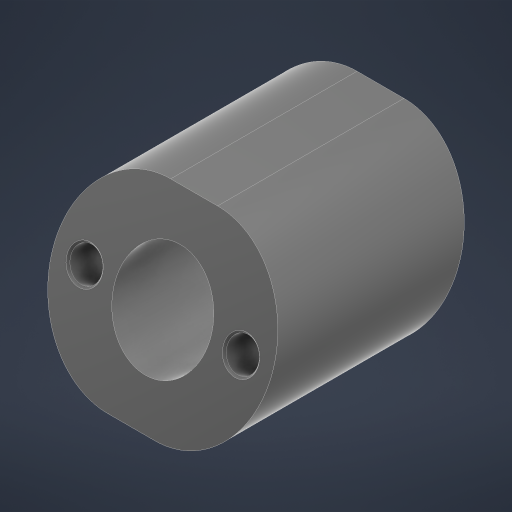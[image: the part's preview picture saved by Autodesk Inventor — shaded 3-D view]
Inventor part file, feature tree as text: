
AUTODESK INVENTOR PART (.ipt)
format: ipt  version: 2024.1 (Build 281209000, 209)  size: 284,160 bytes
history: native  units: mm
features: extrude x6, sketch x6, fillet x2, chamfer x1
ambient origin geometry x8: Origin, YZ Plane, XZ Plane, XY Plane, X Axis, Y Axis, Z Axis, Center Point
bodies: Solid1 (feature_tree)
feature tree (15):
  extrude  "Extrusion1"  Depth=3.490659mm
  extrude  "Extrusion2"  Depth=22.4mm
  extrude  "Extrusion3"  Depth=2.0mm
  fillet  "Fillet1"  Radius=6.0mm
  fillet  "Fillet2"  Radius=6.0mm
  extrude  "Extrusion4"  Depth=11.5mm
  extrude  "Extrusion5"  Depth=11.0mm
  extrude  "Extrusion6"  Depth=2.0mm
  chamfer  "Chamfer1"  Distance=28.0mm
  sketch  "Sketch1"  dims[d1=37.5mm d2=3.490659mm]
  sketch  "Sketch2"  dims[d3=2.0mm d4=22.4mm]
  sketch  "Sketch3"  dims[d5=37.5mm d6=2.0mm d7=6.0mm d8=6.0mm]
  sketch  "Sketch4"  dims[d9=11.5mm d10=11.5mm]
  sketch  "Sketch5"  dims[d13=11.0mm d14=11.0mm]
  sketch  "Sketch6"  dims[d15=4.875mm d16=4.875mm d17=28.0mm d18=0.0mm d19=7.875mm d20=0.0mm d21=7.875mm d22=0.0mm d23=6.125mm d24=11.0mm d25=20.0mm d26=4.0mm d27=4.0mm d28=8.0mm d29=0.0mm d30=20.0mm d31=4.0mm d32=4.0mm d33=8.0mm d34=0.0mm d35=4.0mm d36=4.25mm d37=0.0mm d38=0.25mm d39=2.0mm d40=45.0deg]
